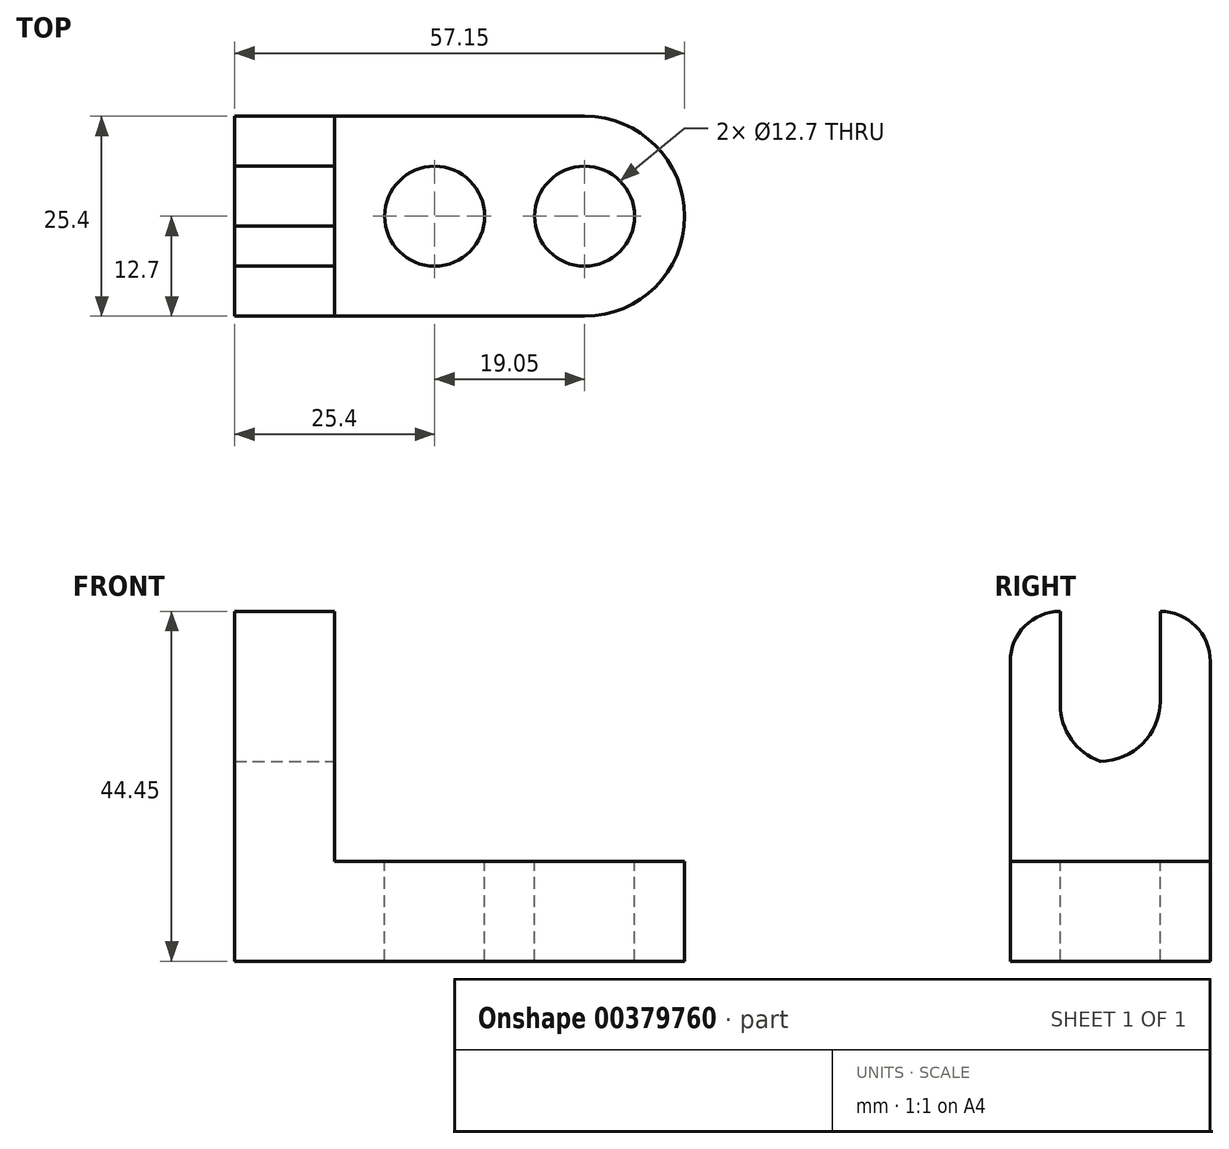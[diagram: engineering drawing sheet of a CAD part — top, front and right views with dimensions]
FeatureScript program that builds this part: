
annotation { "Feature Type Name" : "Feature", "Feature Type Description" : "" }
export const myFeature = defineFeature(function(context is Context, id is Id, definition is map)
    precondition{}
    {
        {
            var Q0;
            Q0=qCreatedBy(makeId("Front.planeOp"),FACE);
            var sketch = newSketch(context, id + "F0", { "sketchPlane" : qUnion([Q0])});
            skLineSegment(sketch, "E0", {"start": v(57.15, 0) * mm, "end": v(0, 0) * mm});
            skLineSegment(sketch, "E1", {"start": v(0, 0) * mm, "end": v(0, 44.45) * mm});
            skLineSegment(sketch, "E2", {"start": v(0, 44.45) * mm, "end": v(12.7, 44.45) * mm});
            skLineSegment(sketch, "E3", {"start": v(12.7, 44.45) * mm, "end": v(12.7, 12.7) * mm});
            skLineSegment(sketch, "E4", {"start": v(12.7, 12.7) * mm, "end": v(57.15, 12.7) * mm});
            skLineSegment(sketch, "E5", {"start": v(57.15, 12.7) * mm, "end": v(57.15, 0) * mm});
            skSolve(sketch);
        }
        {
            var Q0;
            Q0 = qSketchRegion(id + "F0", true);
            extrude(context, id + "F1", {"entities" : qUnion([Q0]), "depth" : 25.4 * mm});
        }
        {
            var Q0;
            Q0=makeQuery(id+"F1.opExtrude","CAP_EDGE",EDGE,{"disambiguationData":[OSD([sQuery(id+"F0.wireOp",EDGE,"E5")])],"isStart":false});
            fillet(context, id + "F2", {"entities" : qUnion([Q0]), "radius" : 12.7 * mm, "tangentPropagation" : true, "allowEdgeOverflow" : false});
        }
        {
            var Q0;
            Q0=makeQuery(id+"F1.opExtrude","CAP_EDGE",EDGE,{"disambiguationData":[OSD([sQuery(id+"F0.wireOp",EDGE,"E5")])],"isStart":true});
            fillet(context, id + "F3", {"entities" : qUnion([Q0]), "radius" : 12.7 * mm, "tangentPropagation" : true, "allowEdgeOverflow" : false});
        }
        {
            var Q0;
            Q0=makeQuery(id+"F1.opExtrude","SWEPT_FACE",FACE,{"disambiguationData":[OSD([sQuery(id+"F0.wireOp",EDGE,"E4")])]});
            var sketch = newSketch(context, id + "F4", { "sketchPlane" : qUnion([Q0])});
            skCircle(sketch, "E6", {"center": v(44.45, -12.7) * mm, "radius": 6.35 * mm});
            skCircle(sketch, "E7", {"center": v(25.4, -12.7) * mm, "radius": 6.35 * mm});
            skPoint(sketch, "E7.centerSnap0", {"position": v(12.7, -12.7) * mm});
            skSolve(sketch);
        }
        {
            var Q0;
            Q0 = qSketchRegion(id + "F4", true);
            extrude(context, id + "F5", {"entities" : qUnion([Q0]), "operationType" : NewBodyOperationType.REMOVE, "oppositeDirection" : true, "depth" : 25.4 * mm});
        }
        {
            var Q0;
            Q0=makeQuery(id+"F1.opExtrude","CAP_EDGE",EDGE,{"disambiguationData":[OSD([sQuery(id+"F0.wireOp",EDGE,"E2")])],"isStart":false});
            fillet(context, id + "F6", {"entities" : qUnion([Q0]), "radius" : 6.35 * mm, "tangentPropagation" : true, "allowEdgeOverflow" : false});
        }
        {
            var Q0;
            Q0=makeQuery(id+"F1.opExtrude","CAP_EDGE",EDGE,{"disambiguationData":[OSD([sQuery(id+"F0.wireOp",EDGE,"E2")])],"isStart":true});
            fillet(context, id + "F7", {"entities" : qUnion([Q0]), "radius" : 6.35 * mm, "tangentPropagation" : true, "allowEdgeOverflow" : false});
        }
        {
            var Q0;
            Q0=makeQuery(id+"F1.opExtrude","SWEPT_FACE",FACE,{"disambiguationData":[OSD([sQuery(id+"F0.wireOp",EDGE,"E3")])]});
            var sketch = newSketch(context, id + "F8", { "sketchPlane" : qUnion([Q0])});
            skLineSegment(sketch, "E8", {"start": v(-19.05, 44.45) * mm, "end": v(-6.35, 44.45) * mm});
            skLineSegment(sketch, "E9", {"start": v(-6.35, 44.45) * mm, "end": v(-6.35, 25.4) * mm});
            skLineSegment(sketch, "E10", {"start": v(-6.35, 25.4) * mm, "end": v(-19.05, 25.4) * mm});
            skLineSegment(sketch, "E11", {"start": v(-19.05, 25.4) * mm, "end": v(-19.05, 44.45) * mm});
            skSolve(sketch);
        }
        {
            var Q0;
            Q0 = qSketchRegion(id + "F8", true);
            extrude(context, id + "F9", {"entities" : qUnion([Q0]), "operationType" : NewBodyOperationType.REMOVE, "oppositeDirection" : true, "depth" : 25.4 * mm});
        }
        {
            var Q0;
            Q0=makeQuery(id+"F9.boolean.opBoolean","COPY",EDGE,{"derivedFrom":makeQuery(id+"F9.opExtrude","SWEPT_EDGE",EDGE,{"disambiguationData":[OSD([sQuery(id+"F8.wireOp",EDGE,"E9"),sQuery(id+"F8.wireOp",EDGE,"E10")])]})});
            fillet(context, id + "F10", {"entities" : qUnion([Q0]), "radius" : 7.62 * mm, "tangentPropagation" : true, "allowEdgeOverflow" : false});
        }
        {
            var Q0;
            Q0=makeQuery(id+"F9.boolean.opBoolean","COPY",EDGE,{"derivedFrom":makeQuery(id+"F9.opExtrude","SWEPT_EDGE",EDGE,{"disambiguationData":[OSD([sQuery(id+"F8.wireOp",EDGE,"E10"),sQuery(id+"F8.wireOp",EDGE,"E11")])]})});
            fillet(context, id + "F11", {"entities" : qUnion([Q0]), "radius" : 7.62 * mm, "tangentPropagation" : true, "allowEdgeOverflow" : false});
        }
    });
